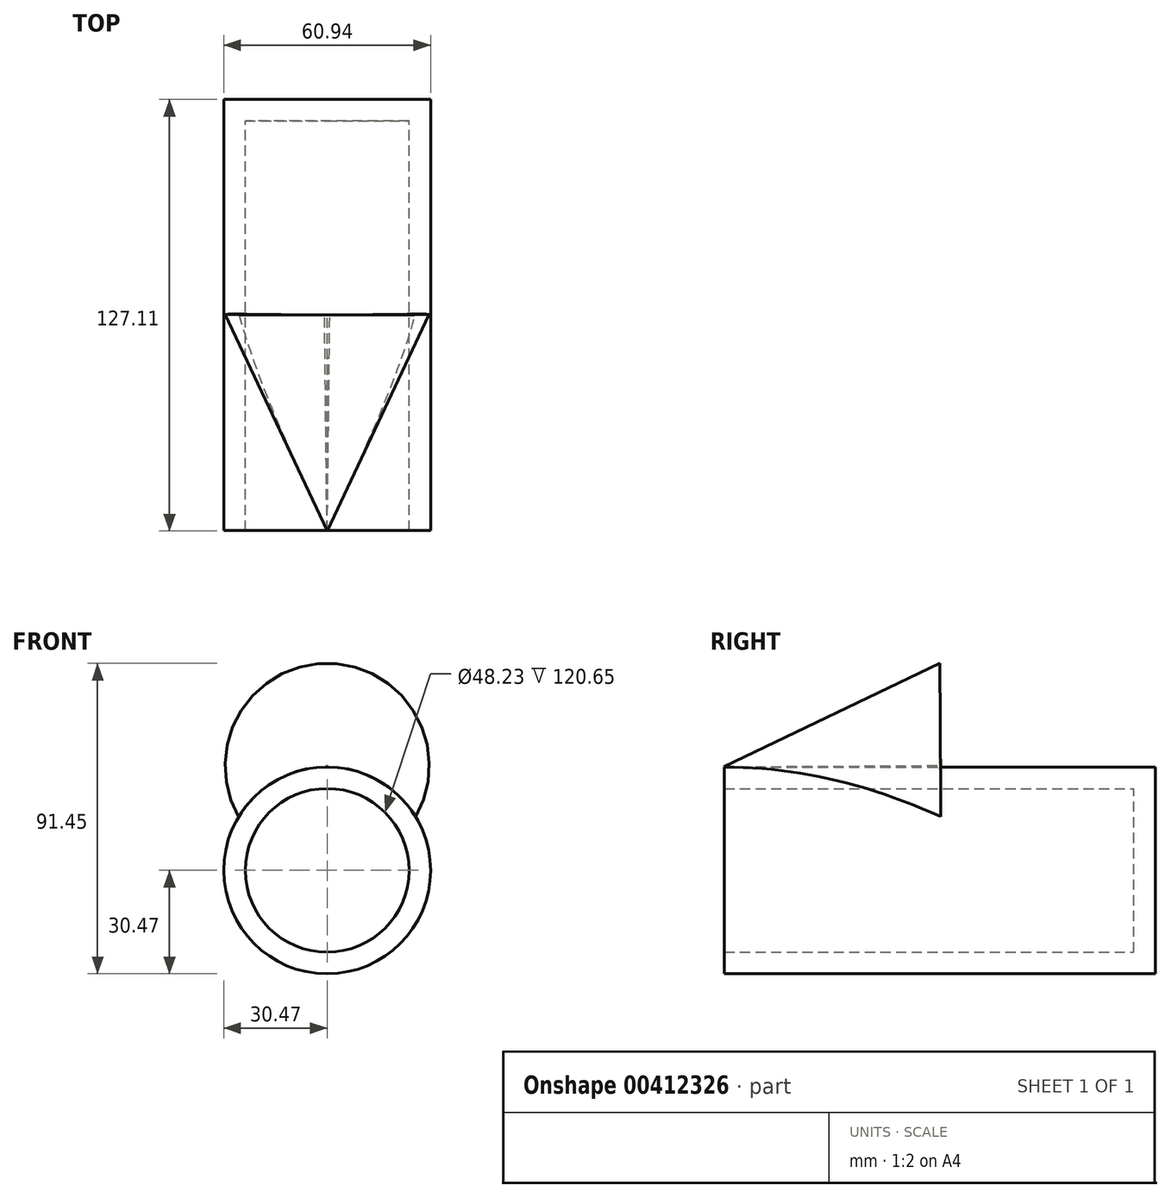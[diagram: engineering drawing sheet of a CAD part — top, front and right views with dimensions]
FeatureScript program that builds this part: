
annotation { "Feature Type Name" : "Feature", "Feature Type Description" : "" }
export const myFeature = defineFeature(function(context is Context, id is Id, definition is map)
    precondition{}
    {
        {
            var Q0;
            Q0=qCreatedBy(makeId("Front.planeOp"),FACE);
            var sketch = newSketch(context, id + "F0", { "sketchPlane" : qUnion([Q0])});
            skCircle(sketch, "E0", {"center": v(0, 0) * mm, "radius": 30.47 * mm});
            skSolve(sketch);
        }
        {
            var Q0;
            Q0=makeQuery(id+"F0.imprint","IMPRINT",FACE,{"disambiguationData":[TD([[makeQuery(id+"F0.imprint","IMPRINT",EDGE,{"derivedFrom":sQuery(id+"F0.wireOp",EDGE,"E0")}),1.0]])]});
            extrude(context, id + "F1", {"entities" : qUnion([Q0]), "endBound" : BoundingType.SYMMETRIC, "depth" : 127 * mm});
        }
        {
            var Q0;
            Q0=makeQuery(id+"F1.opExtrude","CAP_FACE",FACE,{"disambiguationData":[OSD([sQuery(id+"F0.wireOp",EDGE,"E0")])],"isStart":false});
            shell(context, id + "F2", {"entities" : qUnion([Q0]), "thickness" : 6.35 * mm});
        }
        {
            var Q0;
            Q0=qCreatedBy(makeId("Right.planeOp"),FACE);
            var sketch = newSketch(context, id + "F3", { "sketchPlane" : qUnion([Q0])});
            skLineSegment(sketch, "E1", {"start": v(0, 30.9) * mm, "end": v(0, 60.98) * mm});
            skLineSegment(sketch, "E2", {"start": v(0, 60.98) * mm, "end": v(-63.6, 30.5) * mm});
            skLineSegment(sketch, "E3", {"start": v(-63.6, 30.5) * mm, "end": v(0, 30.9) * mm});
            skSolve(sketch);
        }
        {
            var Q0;
            Q0=makeQuery(id+"F3.imprint","IMPRINT",FACE,{"disambiguationData":[TD([[makeQuery(id+"F3.imprint","IMPRINT",EDGE,{"derivedFrom":sQuery(id+"F3.wireOp",EDGE,"E1")}),1.0]])]});
            var Q1;
            Q1=sQuery(id+"F3.wireOp",EDGE,"E3");
            revolve(context, id + "F4", {"operationType" : NewBodyOperationType.ADD, "entities" : qUnion([Q0]), "axis" : qUnion([Q1]), "revolveType" : RevolveType.SYMMETRIC, "angle" : 240 * degree});
        }
    });
